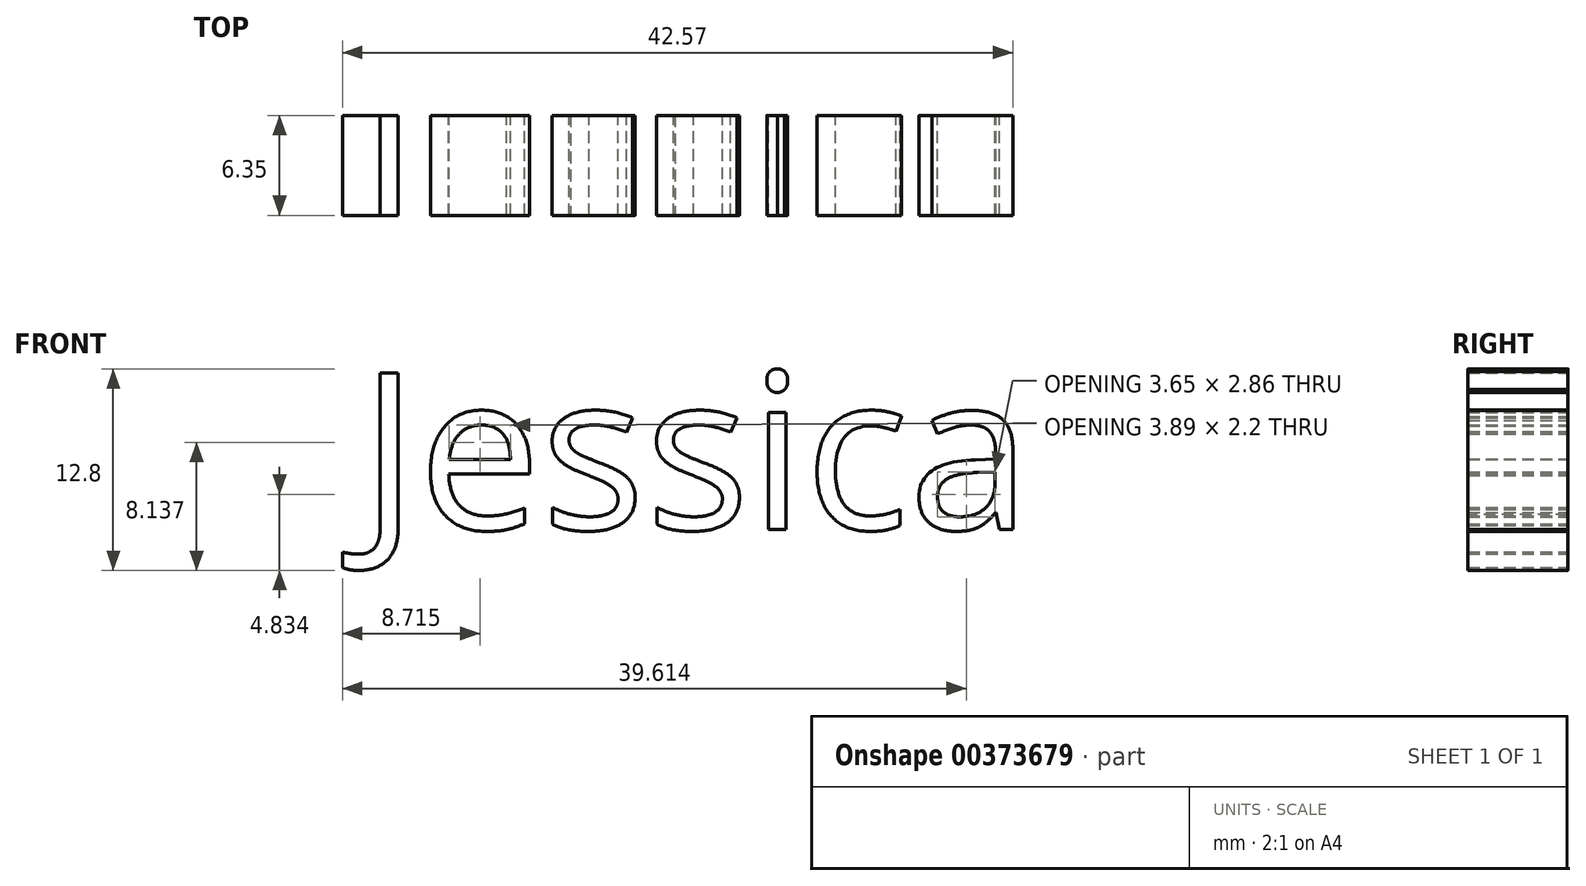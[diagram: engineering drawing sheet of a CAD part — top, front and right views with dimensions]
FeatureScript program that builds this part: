
annotation { "Feature Type Name" : "Feature", "Feature Type Description" : "" }
export const myFeature = defineFeature(function(context is Context, id is Id, definition is map)
    precondition{}
    {
        {
            var Q0;
            Q0=qCreatedBy(makeId("Front.planeOp"),FACE);
            var sketch = newSketch(context, id + "F0", { "sketchPlane" : qUnion([Q0])});
            skText(sketch, "E0", { "text": "Jessica", "fontName": "OpenSans-Regular.ttf"});
            const initialGuessF0  = {"E0": [-0.01337, 0.00716, 1, 0, 0.01]};
            skSetInitialGuess(sketch, initialGuessF0);
            skSolve(sketch);
        }
        {
            var Q0;
            Q0 = qSketchRegion(id + "F0", true);
            extrude(context, id + "F1", {"entities" : qUnion([Q0]), "depth" : 6.35 * mm});
        }
    });
